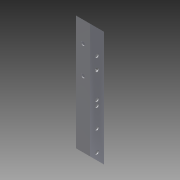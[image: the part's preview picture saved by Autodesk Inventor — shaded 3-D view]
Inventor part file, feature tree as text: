
AUTODESK INVENTOR PART (.ipt)
format: ipt  version: 2013 (Build 170138000, 138)  size: 130,048 bytes
history: native  units: in
note: dims shown in document units (in); Inventor stores cm internally (conversion verified against a paired STEP export)
features: reference x8, extrude x7, sketch x7
ambient origin geometry x8: Origin, YZ Plane, XZ Plane, XY Plane, X Axis, Y Axis, Z Axis, Center Point
bodies: Solid1 (feature_tree)
feature tree (22):
  extrude  "Extrusion1"  Depth=1.0in
  extrude  "Extrusion2"  Depth=10.0in TaperAngle=0.0deg
  extrude  "Extrusion3"  Depth=1.0in TaperAngle=0.0deg
  extrude  "Extrusion4"  Depth=1.0in TaperAngle=0.0deg
  extrude  "Extrusion5"  Depth=0.75in
  extrude  "Extrusion6"  Depth=1.0in TaperAngle=0.0deg
  extrude  "Extrusion7"  [1 undecoded]
  sketch  "Sketch1"  dims[d0=1.0in d2=1.0in]
  sketch  "Sketch2"  dims[d3=0.0625in d4=10.0in d5=0.0in]
  sketch  "Sketch3"  dims[d6=1.0in d7=1.0in d8=0.0in]
  sketch  "Sketch4"  dims[d9=1.0in d10=0.0in d11=1.0in d12=0.0in]
  reference  "Reference1"
  reference  "Reference2"
  sketch  "Sketch5"  dims[d13=1.0in d14=0.75in]
  reference  "Reference3"
  reference  "Reference4"
  sketch  "Sketch6"  dims[d15=1.0in d16=0.0in d17=1.0in d18=0.0in]
  reference  "Reference5"
  reference  "Reference6"
  sketch  "Sketch7"  dims[d19=1.0in d20=0.0in]
  reference  "Reference7"
  reference  "Reference8"
note: 1 required parameter value undecoded (feature->parameter linkage not recoverable at this tier; creation-order binding heuristic only, values carry confidence <= 0.55)
